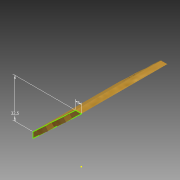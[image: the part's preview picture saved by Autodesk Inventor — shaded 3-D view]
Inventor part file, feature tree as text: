
AUTODESK INVENTOR PART (.ipt)
format: ipt  version: 2014 (Build 180170000, 170)  size: 155,648 bytes
history: native  units: mm
features: extrude x5, sketch x4
ambient origin geometry x8: Origin, YZ Plane, XZ Plane, XY Plane, X Axis, Y Axis, Z Axis, Center Point
bodies: Solid1 (feature_tree)
feature tree (9):
  extrude  "Extrusion1"  Depth=70.0mm TaperAngle=0.0deg
  sketch  "Sketch2"  dims[d7=25.0mm d8=5.0mm]
  extrude  "Extrusion2"  Depth=5.0mm
  extrude  "Extrusion3"  Depth=10.0mm
  extrude  "Extrusion4"  Depth=2.0mm
  extrude  "Extrusion5"  Depth=5.0mm
  sketch  "Sketch1"  dims[d2=5.0mm d5=70.0mm d6=0.0mm]
  sketch  "Sketch3"  dims[d9=10.0mm d10=1.5mm]
  sketch  "Sketch4"  dims[d11=8.0mm d12=2.0mm d13=5.0mm d14=7.0mm d15=2.0mm d16=35.0mm d17=5.0mm d18=0.0mm d19=5.0mm d20=0.0mm d25=90.0deg d28=10.0mm d32=18.45659mm d33=10.0mm d34=5.0mm d35=0.0mm d41=5.0mm d42=0.0mm d46=32.5mm]
